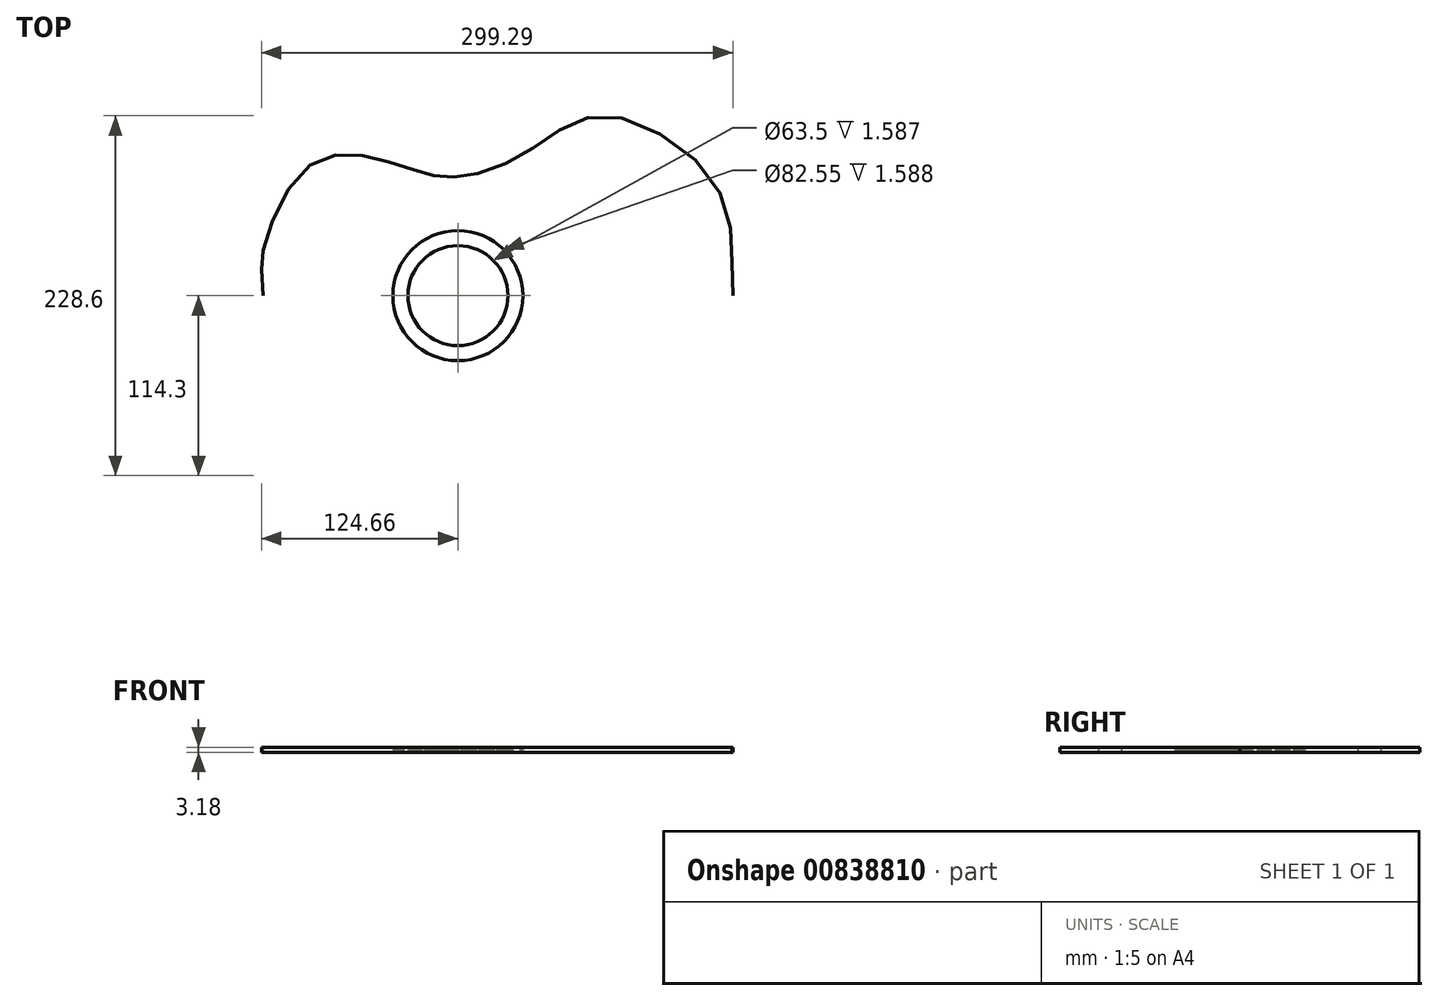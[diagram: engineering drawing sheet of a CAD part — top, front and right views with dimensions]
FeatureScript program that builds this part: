
annotation { "Feature Type Name" : "Feature", "Feature Type Description" : "" }
export const myFeature = defineFeature(function(context is Context, id is Id, definition is map)
    precondition{}
    {
        {
            var Q0;
            Q0=qCreatedBy(makeId("Top.planeOp"),FACE);
            var sketch = newSketch(context, id + "F0", { "sketchPlane" : qUnion([Q0])});
            skCircle(sketch, "E0", {"center": v(0, 0) * mm, "radius": 31.75 * mm});
            skFitSpline(sketch, "E1", {"points": [v(-123.83, 0) * mm, v(-123.83, -28.13) * mm, v(-96, -81.4) * mm, v(-57.15, -88.27) * mm, v(-22.78, -78.36) * mm, v(0, -75.4) * mm, v(42.93, -90.56) * mm, v(92.08, -114.3) * mm, v(166.2, -65.98) * mm, v(174.63, 0) * mm], "startDerivative": vector(0, -540.72) * mm, "endDerivative": vector(49.2, 458.31) * mm});
            skFitSpline(sketch, "E2.MirrorCS", {"points": [v(-123.83, 0) * mm, v(-123.83, 28.13) * mm, v(-96, 81.4) * mm, v(-57.15, 88.27) * mm, v(-22.78, 78.36) * mm, v(0, 75.4) * mm, v(42.93, 90.56) * mm, v(92.08, 114.3) * mm, v(166.2, 65.98) * mm, v(174.63, 0) * mm], "startDerivative": vector(0, 540.72) * mm, "endDerivative": vector(49.2, -458.31) * mm});
            skSolve(sketch);
        }
        {
            var Q0;
            Q0 = qSketchRegion(id + "F0", true);
            extrude(context, id + "F1", {"entities" : qUnion([Q0]), "endBound" : BoundingType.SYMMETRIC, "depth" : 3.17 * mm, "offsetDistance" : 25.4 * mm});
        }
        {
            var Q0;
            Q0=sQuery(id+"F0.wireOp",VERTEX,"E0.center");
            var Q1;
            Q1=makeQuery(id+"F1.opExtrude","SWEPT_BODY",BODY,{"disambiguationData":[OSD([sQuery(id+"F0.wireOp",EDGE,"E0"),sQuery(id+"F0.wireOp",EDGE,"E1"),sQuery(id+"F0.wireOp",EDGE,"E2.MirrorCS")])]});
            hole(context, id + "F2", {"style" : HoleStyle.SIMPLE, "endStyle" : HoleEndStyle.BLIND, "oppositeDirection" : true, "holeDiameter" : 82.55 * mm, "majorDiameter" : 6.35 * mm, "holeDepth" : 1.59 * mm, "isTappedThrough" : true, "tappedDepth" : 12.7 * mm, "tapClearance" : 3, "startFromSketch" : true, "locations" : qUnion([Q0]), "scope" : qUnion([Q1])});
        }
    });
